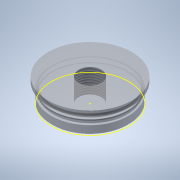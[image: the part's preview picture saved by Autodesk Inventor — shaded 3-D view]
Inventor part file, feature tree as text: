
AUTODESK INVENTOR PART (.ipt)
format: ipt  version: 2022 (Build 260153000, 153)  size: 227,840 bytes
history: native  units: mm
features: sketch x5, extrude x2, plane x1, revolve x1, chamfer x1, fillet x1, hole x1
ambient origin geometry x8: Origin, YZ Plane, XZ Plane, XY Plane, X Axis, Y Axis, Z Axis, Center Point
bodies: Volumenkörper1 (feature_tree)
feature tree (12):
  extrude  "Extrusion1"  Depth=15.0mm TaperAngle=0.0deg
  extrude  "Extrusion2"  Depth=12.0mm TaperAngle=0.0deg
  sketch  "Skizze3"  dims[d6=0.0mm]
  plane  "Arbeitsebene1"
  revolve  "Umdrehung1"
  chamfer  "Fase1"  Distance=1.0mm Angle=45.0deg
  fillet  "Rundung1"  Radius=0.2mm
  hole  "Bohrung1"  [1 undecoded]
  sketch  "Skizze1"  dims[d0=53.0mm d1=15.0mm d2=0.0mm]
  sketch  "Skizze2"  dims[d3=48.8mm d4=12.0mm d5=0.0mm]
  sketch  "Skizze4"  dims[d10=1.0mm]
  sketch  "Skizze5"  dims[d11=90.0deg d12=1.0mm d13=2.0mm d14=45.0deg d15=0.2mm d16=0.3mm d17=14.376mm d18=6.0mm d19=4.0mm d20=2.0mm d21=90.0deg d22=8.0mm d23=20.594885mm d24=0.5mm d25=0.872665mm d26=0.5mm d27=0.872665mm]
note: 1 required parameter value undecoded (feature->parameter linkage not recoverable at this tier; creation-order binding heuristic only, values carry confidence <= 0.55)
